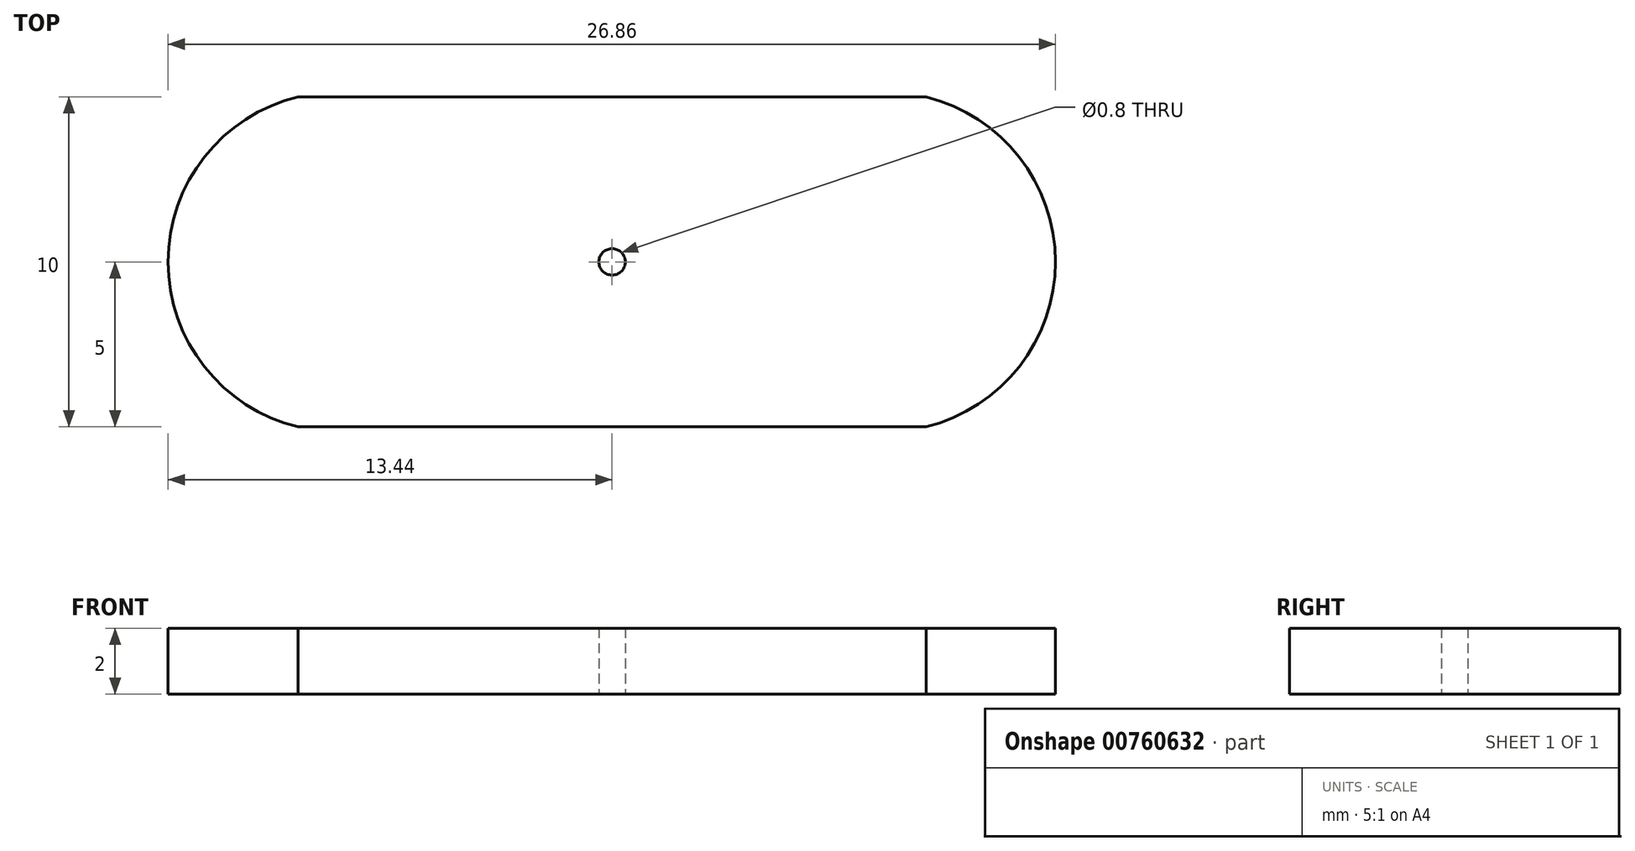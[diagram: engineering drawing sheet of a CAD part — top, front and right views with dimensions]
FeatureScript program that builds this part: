
annotation { "Feature Type Name" : "Feature", "Feature Type Description" : "" }
export const myFeature = defineFeature(function(context is Context, id is Id, definition is map)
    precondition{}
    {
        {
            var Q0;
            Q0=qCreatedBy(makeId("Top.planeOp"),FACE);
            var sketch = newSketch(context, id + "F0", { "sketchPlane" : qUnion([Q0])});
            skLineSegment(sketch, "E0.bottom", {"start": v(9.5, -5) * mm, "end": v(-9.5, -5) * mm});
            skLineSegment(sketch, "E0.top", {"start": v(9.5, 5) * mm, "end": v(-9.5, 5) * mm});
            skPoint(sketch, "E0.middle", {"position": v(0, 0) * mm});
            skLineSegment(sketch, "E1", {"start": v(-13.5, 16.08) * mm, "end": v(-13.5, -14.56) * mm, "construction": true});
            skLineSegment(sketch, "E2", {"start": v(13.5, 17.66) * mm, "end": v(13.5, -14.65) * mm, "construction": true});
            skArc(sketch, "E3", {"start": v(9.5, -5) * mm, "mid": v(13.42, 0) * mm, "end": v(9.5, 5) * mm});
            skArc(sketch, "E4", {"start": v(-9.5, 5) * mm, "mid": v(-13.44, 0) * mm, "end": v(-9.5, -5) * mm});
            skCircle(sketch, "E5", {"center": v(0, 0) * mm, "radius": 0.4 * mm});
            skSolve(sketch);
        }
        {
            var Q0;
            Q0=makeQuery(id+"F0.imprint","IMPRINT",FACE,{"disambiguationData":[TD([[makeQuery(id+"F0.imprint","IMPRINT",EDGE,{"derivedFrom":sQuery(id+"F0.wireOp",EDGE,"E0.bottom")}),-1.0]])]});
            extrude(context, id + "F1", {"entities" : qUnion([Q0]), "depth" : 2 * mm, "offsetDistance" : 25 * mm});
        }
    });
